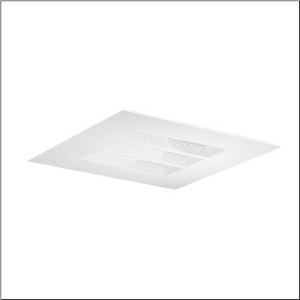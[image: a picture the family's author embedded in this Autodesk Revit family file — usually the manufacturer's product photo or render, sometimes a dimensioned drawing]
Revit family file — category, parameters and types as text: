
# Revit family: taris_r__21_51mt1ld0jhgedc02_ab78
name_source: partatom
category: Lighting Fixtures
units: mm (PartAtom-declared; Revit-internal decimal feet)

## family parameters
Cut with Voids When Loaded = No
Host = Face
Light Source = No
Part Type = Normal
Room Calculation Point = No
Round Connector Dimension = Use Diameter
Shared = No

## types (1)
- --- (1 x LED, 4620 lm, 27.4 W, 4000K)
    Apparent Load = 27 VA
    CIE Flux Codes = 79 97 100 100 100
    Color Rendering = 80
    Color Temperature = 4000K
    Default Elevation = 1800 mm
    Description = Taris® 21, office luminaire, primary anti-glare with micro louvre, primary optical cover: axial lens, of PMMA, structured, CAT 2 (L<= 1500cd/m²), light emission: direct distribution, primary light characteristic: symmetric, installation type: lay-in mounting, LED rated luminous flux: 4.620 lm, light colour: 840, colour temperature: 4000K, control gear: ECG DALI, with terminal, 5-pole, mains connection: 230V, AC, 50Hz, rated input power: 27W, housing, luminaire housing, of plastic, traffic white (RAL 9016), module: M600, length: 597 mm, width: 597 mm, height: 42mm, protection rating (complete): IP20, insulation class (complete): insulation class I (protective earthing), certification: CE, ENEC, VDE, protection symbol: F, impact resistance: IK02, permissible ambient temperature for indoor applications: 0..+35°C, standard: EN 50419, packaging unit: 1 piece
    Height = 0 mm  [stored 0 ft]
    Lamp = 1 x LED
    Lamp Light Flux = 4620 lm
    Lamp Power = 27.4 W
    Lamp count = 1
    Length = 597 mm
    Luminous efficacy = 169 lm/W
    Manufacturer = Siteco
    ModVariant = No
    Model = 51MT1LD0JHGEDC02
    Mounting Place = Ceiling
    Mounting Type = Recessed
    Number of Poles = 1
    OnlyDefault = Yes
    Power Factor = 1
    Product Name = Taris® 21
    Product group = office luminaire | ceiling recessed
    ProductGroupID = 400
    Protection Class = Protection class I
    Protection Degree = IP 20
    RLX_Detail_Level = 1
    RlxData = <blob elided: 23317 chars, md5=38ac334c>
    Socket = socket
    Standby Power = 0 W
    System Light Flux = 4620 lm
    System Power = 27 W
    Type Comments = factory setting: luminous flux: 100 % | dim-lin: 254 | 250 mA
    Type Image = l_1004820.jpg
    URL = http://relux.com
    VarID = @adj_130449
    Voltage = 0 V
    Weight = 0.00 kg
    Width = 597 mm

note: [stored X ft] marks values corroborated as IEEE doubles in the binary element streams (Revit-internal decimal feet)

## geometry (parser evidence)
native form markers: Blend x4, Sweep x13
no freeform markers — native parametric forms only
